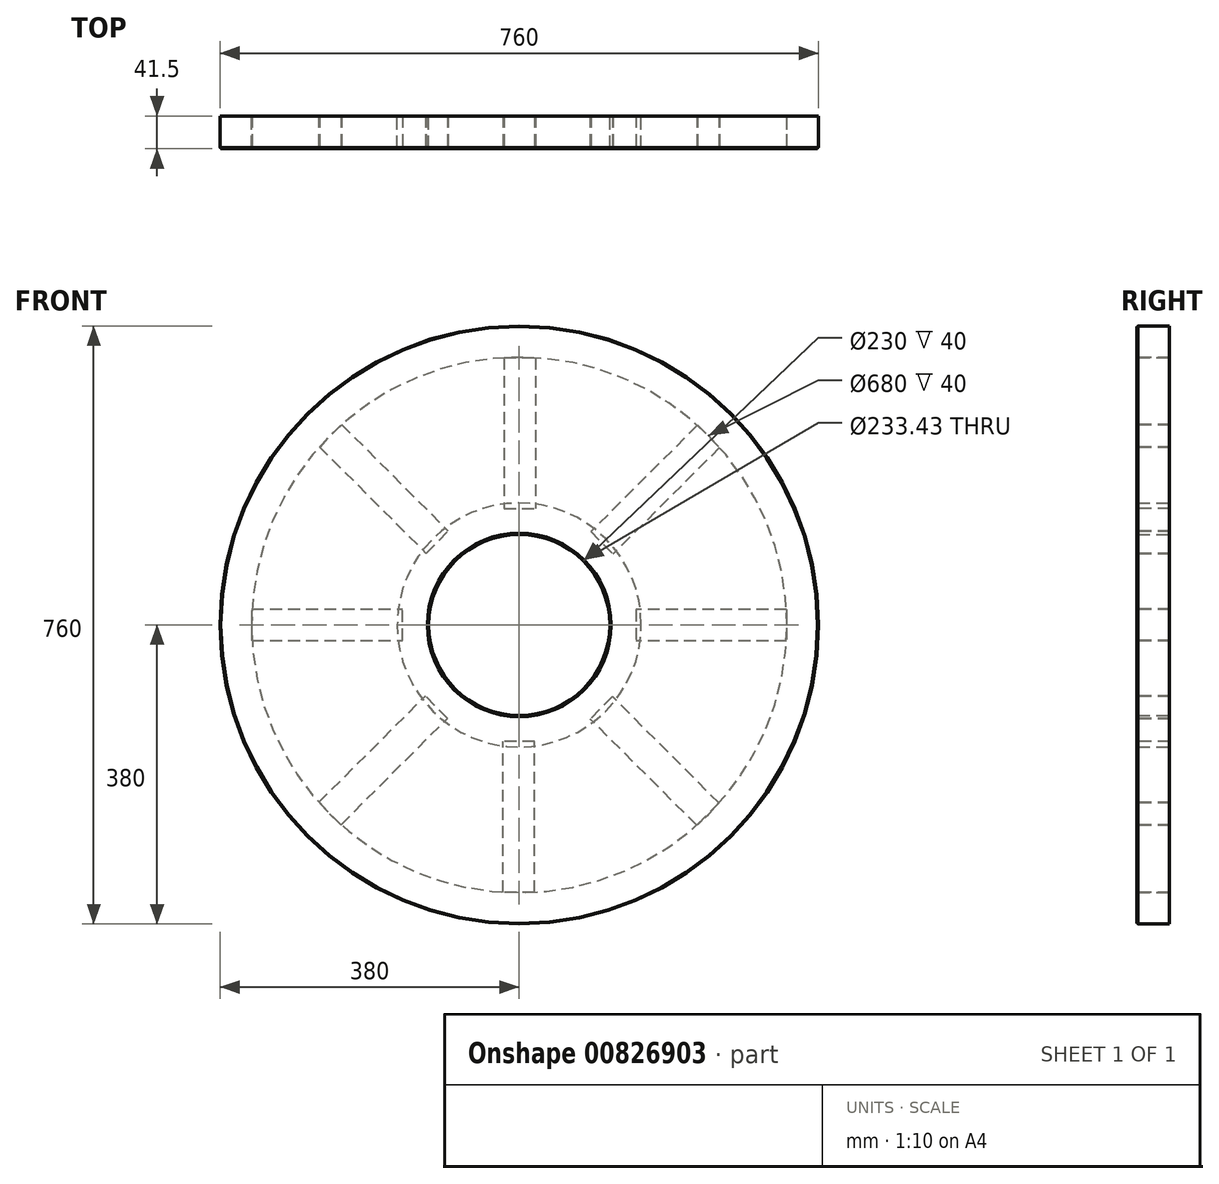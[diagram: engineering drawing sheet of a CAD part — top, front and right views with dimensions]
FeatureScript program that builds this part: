
annotation { "Feature Type Name" : "Feature", "Feature Type Description" : "" }
export const myFeature = defineFeature(function(context is Context, id is Id, definition is map)
    precondition{}
    {
        {
            var Q0;
            Q0=qCreatedBy(makeId("Front.planeOp"),FACE);
            var sketch = newSketch(context, id + "F0", { "sketchPlane" : qUnion([Q0])});
            skCircle(sketch, "E0", {"center": v(0, 0) * mm, "radius": 115 * mm});
            skCircle(sketch, "E1", {"center": v(0, 0) * mm, "radius": 380 * mm});
            skCircle(sketch, "E2.0", {"center": v(0, 0) * mm, "radius": 340 * mm});
            skCircle(sketch, "E3.0", {"center": v(0, 0) * mm, "radius": 155 * mm});
            skSolve(sketch);
        }
        {
            var Q0;
            Q0 = qSketchRegion(id + "F0", true);
            var Q1;
            Q1=makeQuery(id+"F0.imprint","IMPRINT",FACE,{"disambiguationData":[TD([[makeQuery(id+"F0.imprint","IMPRINT",EDGE,{"derivedFrom":sQuery(id+"F0.wireOp",EDGE,"E0")}),-1.0]])]});
            extrude(context, id + "F1", {"entities" : qUnion([Q0, Q1]), "depth" : 40 * mm, "offsetDistance" : 25 * mm});
        }
        {
            var Q0;
            Q0=makeQuery(id+"F1.opExtrude","CAP_FACE",FACE,{"disambiguationData":[OSD([sQuery(id+"F0.wireOp",EDGE,"E1"),sQuery(id+"F0.wireOp",EDGE,"E2.0")])],"isStart":false});
            var sketch = newSketch(context, id + "F2", { "sketchPlane" : qUnion([Q0])});
            skLineSegment(sketch, "E4", {"start": v(0, 584.2) * mm, "end": v(0, 0) * mm});
            skLineSegment(sketch, "E5.0", {"start": v(-20, 584.2) * mm, "end": v(-20, 0) * mm});
            skLineSegment(sketch, "E6.0", {"start": v(20, 584.2) * mm, "end": v(20, 0) * mm});
            skSolve(sketch);
        }
        {
            var Q0;
            {var subQ0=sQuery(id+"F2.wireOp",EDGE,"E5.0");var subQ1=makeQuery(id+"F1.opExtrude","CAP_EDGE",EDGE,{"disambiguationData":[OSD([sQuery(id+"F0.wireOp",EDGE,"E1")])],"isStart":false});var subQ2=makeQuery(id+"F2.imprint","INTERSECT",VERTEX,{"derivedFrom":[subQ1,subQ0]});Q0=makeQuery(id+"F2.imprint","IMPRINT",FACE,{"disambiguationData":[TD([[makeQuery(id+"F2.imprint","IMPRINT",EDGE,{"disambiguationData":[TD([[subQ2,-1.0]])],"derivedFrom":subQ0}),-1.0]])]});}
            var sketch = newSketch(context, id + "F3", { "sketchPlane" : qUnion([Q0])});
            skLineSegment(sketch, "E7.bottom", {"start": v(-19.4, 339.5) * mm, "end": v(20.6, 339.5) * mm});
            skLineSegment(sketch, "E7.top", {"start": v(-19.4, 148.12) * mm, "end": v(20.6, 148.12) * mm});
            skLineSegment(sketch, "E7.left", {"start": v(-19.4, 339.5) * mm, "end": v(-19.4, 148.12) * mm});
            skLineSegment(sketch, "E7.right", {"start": v(20.6, 339.5) * mm, "end": v(20.6, 148.12) * mm});
            skSolve(sketch);
        }
        {
            var Q0;
            Q0 = qSketchRegion(id + "F3", true);
            extrude(context, id + "F4", {"entities" : qUnion([Q0]), "oppositeDirection" : true, "depth" : 40 * mm, "offsetDistance" : 25 * mm});
        }
        {
            var Q0;
            Q0=qCreatedBy(makeId("Right.planeOp"),FACE);
            var sketch = newSketch(context, id + "F5", { "sketchPlane" : qUnion([Q0])});
            skLineSegment(sketch, "E8", {"start": v(134.09, 0) * mm, "end": v(-72.33, 0) * mm});
            skSolve(sketch);
        }
        {
            var Q0;
            Q0=makeQuery(id+"F4.opExtrude","SWEPT_BODY",BODY,{"disambiguationData":[OSD([sQuery(id+"F3.wireOp",EDGE,"E7.bottom"),sQuery(id+"F3.wireOp",EDGE,"E7.top"),sQuery(id+"F3.wireOp",EDGE,"E7.left"),sQuery(id+"F3.wireOp",EDGE,"E7.right")])]});
            var Q1;
            Q1=sQuery(id+"F5.wireOp",EDGE,"E8");
            circularPattern(context, id + "F6", {"entities" : qUnion([Q0]), "axis" : qUnion([Q1]), "angle" : 360 * degree, "instanceCount" : 8, "equalSpace" : true});
        }
        {
            var Q0;
            {var subQ0=sQuery(id+"F2.wireOp",EDGE,"E5.0");var subQ1=makeQuery(id+"F1.opExtrude","CAP_EDGE",EDGE,{"disambiguationData":[OSD([sQuery(id+"F0.wireOp",EDGE,"E1")])],"isStart":false});var subQ2=makeQuery(id+"F2.imprint","INTERSECT",VERTEX,{"derivedFrom":[subQ1,subQ0]});var subQ14=makeQuery(id+"F2.imprint","IMPRINT",EDGE,{"disambiguationData":[TD([[subQ2,-1.0]])],"derivedFrom":subQ0});Q0=makeQuery(id+"F3.imprint","IMPRINT",FACE,{"disambiguationData":[TD([[makeQuery(id+"F3.imprint","IMPRINT",EDGE,{"derivedFrom":subQ14}),-1.0]])]});}
            var sketch = newSketch(context, id + "F7", { "sketchPlane" : qUnion([Q0])});
            skCircle(sketch, "E9", {"center": v(0, 0) * mm, "radius": 379.06 * mm});
            skCircle(sketch, "E10", {"center": v(0, 0) * mm, "radius": 116.72 * mm});
            skSolve(sketch);
        }
        {
            var Q0;
            Q0 = qSketchRegion(id + "F7", true);
            extrude(context, id + "F8", {"entities" : qUnion([Q0]), "depth" : 1.5 * mm, "offsetDistance" : 25 * mm});
        }
    });
